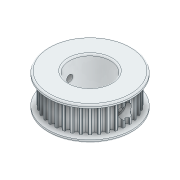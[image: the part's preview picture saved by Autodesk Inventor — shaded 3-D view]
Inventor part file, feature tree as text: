
AUTODESK INVENTOR PART (.ipt)
format: ipt  version: 2020 (Build 240168000, 168)  size: 1,259,520 bytes
history: native  units: in
note: dims shown in document units (in); Inventor stores cm internally (conversion verified against a paired STEP export)
features: extrude x5, sketch x5, plane x2, fillet x2, chamfer x1
ambient origin geometry x8: Origin, YZ Plane, XZ Plane, XY Plane, X Axis, Y Axis, Z Axis, Center Point
bodies: Solid1 (feature_tree)
feature tree (15):
  extrude  "Extrusion1"  Depth=0.3937in
  plane  "Work Plane1"
  extrude  "Extrusion2"  Depth=0.1476in TaperAngle=0.0deg
  extrude  "Extrusion3"  TaperAngle=0.0deg  [1 undecoded]
  plane  "Work Plane2"
  extrude  "Extrusion4"  Depth=0.1476in TaperAngle=0.0deg
  extrude  "Extrusion5"  Depth=0.3937in TaperAngle=0.0deg
  fillet  "Fillet2"  Radius=0.0197in
  fillet  "Fillet3"  Radius=0.0197in
  sketch  "Sketch1"  dims[d0=0.3937in d1=0.0in d3=0.1142in]
  sketch  "Sketch2"  dims[d4=0.1575in d5=0.1476in d6=0.0in]
  sketch  "Sketch3"  dims[d7=0.0748in d8=0.0in d9=0.0in]
  sketch  "Sketch4"  dims[d10=0.1575in d11=0.1476in d12=0.0in]
  sketch  "Sketch5"  dims[d13=0.4803in d14=0.3937in d15=0.0in d16=0.0197in d17=0.0197in]
  chamfer  "Chamfer2"  [1 undecoded]
note: 2 required parameter values undecoded (feature->parameter linkage not recoverable at this tier; creation-order binding heuristic only, values carry confidence <= 0.55)
